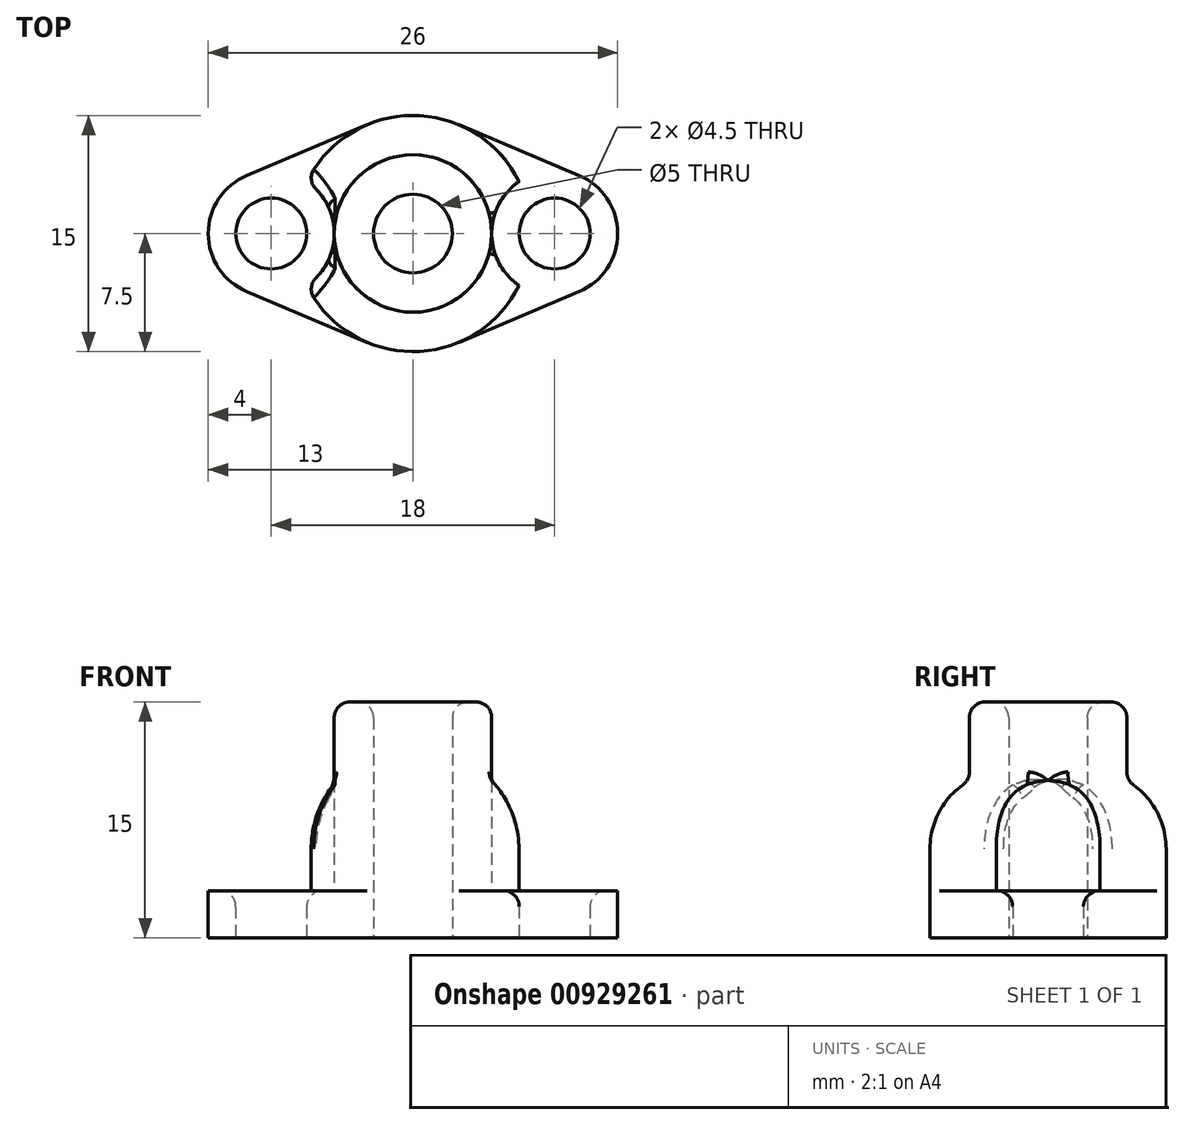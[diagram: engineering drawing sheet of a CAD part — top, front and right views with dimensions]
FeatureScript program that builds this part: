
annotation { "Feature Type Name" : "Feature", "Feature Type Description" : "" }
export const myFeature = defineFeature(function(context is Context, id is Id, definition is map)
    precondition{}
    {
        {
            var Q0;
            Q0=qCreatedBy(makeId("Top.planeOp"),FACE);
            var sketch = newSketch(context, id + "F0", { "sketchPlane" : qUnion([Q0])});
            skCircle(sketch, "E0", {"center": v(0, 0) * mm, "radius": 7.5 * mm});
            skCircle(sketch, "E1", {"center": v(0, 0) * mm, "radius": 5 * mm});
            skCircle(sketch, "E2", {"center": v(0, 0) * mm, "radius": 2.5 * mm});
            skCircle(sketch, "E3", {"center": v(-9, 0) * mm, "radius": 4 * mm});
            skLineSegment(sketch, "E4", {"start": v(-10.56, 3.69) * mm, "end": v(-2.92, 6.9) * mm});
            skLineSegment(sketch, "E5", {"start": v(-10.56, -3.69) * mm, "end": v(-2.92, -6.9) * mm});
            skLineSegment(sketch, "E6.MirrorCS", {"start": v(10.56, 3.69) * mm, "end": v(2.92, 6.9) * mm});
            skCircle(sketch, "E7.MirrorC", {"center": v(9, 0) * mm, "radius": 4 * mm});
            skLineSegment(sketch, "E8.MirrorCS", {"start": v(10.56, -3.69) * mm, "end": v(2.92, -6.9) * mm});
            skCircle(sketch, "E9", {"center": v(-9, 0) * mm, "radius": 2.25 * mm});
            skCircle(sketch, "E10.MirrorC", {"center": v(9, 0) * mm, "radius": 2.25 * mm});
            skSolve(sketch);
        }
        {
            var Q0;
            Q0=makeQuery(id+"F0.imprint","IMPRINT",FACE,{"disambiguationData":[TD([[makeQuery(id+"F0.imprint","IMPRINT",EDGE,{"derivedFrom":sQuery(id+"F0.wireOp",EDGE,"E1")}),1.0]])]});
            extrude(context, id + "F1", {"entities" : qUnion([Q0]), "depth" : 15 * mm, "offsetDistance" : 25 * mm});
        }
        {
            var Q0;
            Q0=makeQuery(id+"F0.imprint","IMPRINT",FACE,{"disambiguationData":[TD([[makeQuery(id+"F0.imprint","IMPRINT",EDGE,{"derivedFrom":sQuery(id+"F0.wireOp",EDGE,"E0")}),1.0]])]});
            extrude(context, id + "F2", {"entities" : qUnion([Q0]), "operationType" : NewBodyOperationType.ADD, "depth" : 10 * mm, "offsetDistance" : 25 * mm});
        }
        {
            var Q0;
            {var subQ0=sQuery(id+"F0.wireOp",EDGE,"E3");var subQ4=sQuery(id+"F0.wireOp",EDGE,"E0");var subQ7=makeQuery(id+"F0.imprint","INTERSECT",VERTEX,{"disambiguationData":[OD(0.0)],"derivedFrom":[subQ4,subQ0]});Q0=makeQuery(id+"F0.imprint","IMPRINT",FACE,{"disambiguationData":[TD([[makeQuery(id+"F0.imprint","IMPRINT",EDGE,{"disambiguationData":[TD([[subQ7,-1.0]])],"derivedFrom":subQ4}),-1.0]])]});}
            var Q1;
            {var subQ0=sQuery(id+"F0.wireOp",EDGE,"E3");var subQ1=sQuery(id+"F0.wireOp",EDGE,"E0");var subQ2=makeQuery(id+"F0.imprint","INTERSECT",VERTEX,{"disambiguationData":[OD(0.0)],"derivedFrom":[subQ1,subQ0]});Q1=makeQuery(id+"F0.imprint","IMPRINT",FACE,{"disambiguationData":[TD([[makeQuery(id+"F0.imprint","IMPRINT",EDGE,{"disambiguationData":[TD([[subQ2,-1.0]])],"derivedFrom":subQ1}),1.0]])]});}
            var Q2;
            {var subQ0=sQuery(id+"F0.wireOp",EDGE,"E5");Q2=makeQuery(id+"F0.imprint","IMPRINT",FACE,{"disambiguationData":[TD([[makeQuery(id+"F0.imprint","IMPRINT",EDGE,{"derivedFrom":subQ0}),1.0]])]});}
            var Q3;
            {var subQ0=sQuery(id+"F0.wireOp",EDGE,"E4");Q3=makeQuery(id+"F0.imprint","IMPRINT",FACE,{"disambiguationData":[TD([[makeQuery(id+"F0.imprint","IMPRINT",EDGE,{"derivedFrom":subQ0}),-1.0]])]});}
            var Q4;
            {var subQ0=sQuery(id+"F0.wireOp",EDGE,"E8.MirrorCS");Q4=makeQuery(id+"F0.imprint","IMPRINT",FACE,{"disambiguationData":[TD([[makeQuery(id+"F0.imprint","IMPRINT",EDGE,{"derivedFrom":subQ0}),-1.0]])]});}
            var Q5;
            {var subQ0=sQuery(id+"F0.wireOp",EDGE,"E7.MirrorC");var subQ2=sQuery(id+"F0.wireOp",EDGE,"E0");var subQ3=makeQuery(id+"F0.imprint","INTERSECT",VERTEX,{"disambiguationData":[OD(0.0)],"derivedFrom":[subQ2,subQ0]});Q5=makeQuery(id+"F0.imprint","IMPRINT",FACE,{"disambiguationData":[TD([[makeQuery(id+"F0.imprint","IMPRINT",EDGE,{"disambiguationData":[TD([[subQ3,1.0]])],"derivedFrom":subQ2}),-1.0]])]});}
            var Q6;
            {var subQ0=sQuery(id+"F0.wireOp",EDGE,"E7.MirrorC");var subQ1=sQuery(id+"F0.wireOp",EDGE,"E0");var subQ4=makeQuery(id+"F0.imprint","INTERSECT",VERTEX,{"disambiguationData":[OD(0.0)],"derivedFrom":[subQ1,subQ0]});Q6=makeQuery(id+"F0.imprint","IMPRINT",FACE,{"disambiguationData":[TD([[makeQuery(id+"F0.imprint","IMPRINT",EDGE,{"disambiguationData":[TD([[subQ4,1.0]])],"derivedFrom":subQ1}),1.0]])]});}
            var Q7;
            {var subQ0=sQuery(id+"F0.wireOp",EDGE,"E6.MirrorCS");Q7=makeQuery(id+"F0.imprint","IMPRINT",FACE,{"disambiguationData":[TD([[makeQuery(id+"F0.imprint","IMPRINT",EDGE,{"derivedFrom":subQ0}),1.0]])]});}
            extrude(context, id + "F3", {"entities" : qUnion([Q0, Q1, Q2, Q3, Q4, Q5, Q6, Q7]), "operationType" : NewBodyOperationType.ADD, "depth" : 3 * mm, "offsetDistance" : 25 * mm});
        }
        {
            var Q0;
            {var subQ0=sQuery(id+"F0.wireOp",EDGE,"E0");var subQ1=makeQuery(id+"F0.imprint","INTERSECT",VERTEX,{"derivedFrom":[subQ0,sQuery(id+"F0.wireOp",EDGE,"E8.MirrorCS")]});var subQ2=makeQuery(id+"F0.imprint","INTERSECT",VERTEX,{"derivedFrom":[subQ0,sQuery(id+"F0.wireOp",EDGE,"E5")]});Q0=makeQuery(id+"F2.opExtrude","CAP_EDGE",EDGE,{"disambiguationData":[OSD([subQ0]),TDD([makeQuery(id+"F0.imprint","IMPRINT",EDGE,{"disambiguationData":[TD([[subQ2,1.0]])],"derivedFrom":subQ0}),makeQuery(id+"F0.imprint","IMPRINT",EDGE,{"disambiguationData":[TD([[subQ2,-1.0]])],"derivedFrom":subQ0}),makeQuery(id+"F0.imprint","IMPRINT",EDGE,{"disambiguationData":[TD([[subQ1,-1.0]])],"derivedFrom":subQ0})])],"isStart":false});}
            var Q1;
            {var subQ0=sQuery(id+"F0.wireOp",EDGE,"E0");var subQ1=makeQuery(id+"F0.imprint","INTERSECT",VERTEX,{"derivedFrom":[subQ0,sQuery(id+"F0.wireOp",EDGE,"E4")]});var subQ2=makeQuery(id+"F0.imprint","INTERSECT",VERTEX,{"derivedFrom":[subQ0,sQuery(id+"F0.wireOp",EDGE,"E6.MirrorCS")]});Q1=makeQuery(id+"F2.opExtrude","CAP_EDGE",EDGE,{"disambiguationData":[OSD([subQ0]),TDD([makeQuery(id+"F0.imprint","IMPRINT",EDGE,{"disambiguationData":[TD([[subQ2,1.0]])],"derivedFrom":subQ0}),makeQuery(id+"F0.imprint","IMPRINT",EDGE,{"disambiguationData":[TD([[subQ1,1.0]])],"derivedFrom":subQ0}),makeQuery(id+"F0.imprint","IMPRINT",EDGE,{"disambiguationData":[TD([[subQ1,-1.0]])],"derivedFrom":subQ0})])],"isStart":false});}
            fillet(context, id + "F4", {"entities" : qUnion([Q0, Q1]), "radius" : 5 * mm, "tangentPropagation" : true, "allowEdgeOverflow" : false});
        }
        {
            var Q0;
            {var subQ0=sQuery(id+"F0.wireOp",EDGE,"E0");var subQ1=makeQuery(id+"F0.imprint","INTERSECT",VERTEX,{"derivedFrom":[subQ0,sQuery(id+"F0.wireOp",EDGE,"E4")]});var subQ2=makeQuery(id+"F0.imprint","INTERSECT",VERTEX,{"derivedFrom":[subQ0,sQuery(id+"F0.wireOp",EDGE,"E6.MirrorCS")]});Q0=makeQuery(id+"F4.opFillet","BLEND_EDGE",EDGE,{"blendedFrom":[makeQuery(id+"F2.opExtrude","CAP_EDGE",EDGE,{"disambiguationData":[OSD([subQ0]),TDD([makeQuery(id+"F0.imprint","IMPRINT",EDGE,{"disambiguationData":[TD([[subQ2,1.0]])],"derivedFrom":subQ0}),makeQuery(id+"F0.imprint","IMPRINT",EDGE,{"disambiguationData":[TD([[subQ1,1.0]])],"derivedFrom":subQ0}),makeQuery(id+"F0.imprint","IMPRINT",EDGE,{"disambiguationData":[TD([[subQ1,-1.0]])],"derivedFrom":subQ0})])],"isStart":false}),makeQuery(id+"F1.opExtrude","SWEPT_FACE",FACE,{"disambiguationData":[OSD([sQuery(id+"F0.wireOp",EDGE,"E1")])]})],"blendedInto":[makeQuery(id+"F1.opExtrude","SWEPT_FACE",FACE,{"disambiguationData":[OSD([sQuery(id+"F0.wireOp",EDGE,"E1")])]})]});}
            var Q1;
            {var subQ0=sQuery(id+"F0.wireOp",EDGE,"E0");Q1=makeQuery(id+"F3.opExtrude","CAP_EDGE",EDGE,{"disambiguationData":[OSD([subQ0]),TDD([makeQuery(id+"F0.imprint","IMPRINT",EDGE,{"disambiguationData":[TD([[makeQuery(id+"F0.imprint","INTERSECT",VERTEX,{"derivedFrom":[subQ0,sQuery(id+"F0.wireOp",EDGE,"E6.MirrorCS")]}),1.0]])],"derivedFrom":subQ0})])],"isStart":false});}
            var Q2;
            {var subQ0=sQuery(id+"F0.wireOp",EDGE,"E0");Q2=makeQuery(id+"F3.opExtrude","CAP_EDGE",EDGE,{"disambiguationData":[OSD([subQ0]),TDD([makeQuery(id+"F0.imprint","IMPRINT",EDGE,{"disambiguationData":[TD([[makeQuery(id+"F0.imprint","INTERSECT",VERTEX,{"derivedFrom":[subQ0,sQuery(id+"F0.wireOp",EDGE,"E4")]}),-1.0]])],"derivedFrom":subQ0})])],"isStart":false});}
            var Q3;
            {var subQ0=sQuery(id+"F0.wireOp",EDGE,"E0");Q3=makeQuery(id+"F3.opExtrude","CAP_EDGE",EDGE,{"disambiguationData":[OSD([subQ0]),TDD([makeQuery(id+"F0.imprint","IMPRINT",EDGE,{"disambiguationData":[TD([[makeQuery(id+"F0.imprint","INTERSECT",VERTEX,{"derivedFrom":[subQ0,sQuery(id+"F0.wireOp",EDGE,"E8.MirrorCS")]}),-1.0]])],"derivedFrom":subQ0})])],"isStart":false});}
            var Q4;
            {var subQ0=sQuery(id+"F0.wireOp",EDGE,"E0");Q4=makeQuery(id+"F3.opExtrude","CAP_EDGE",EDGE,{"disambiguationData":[OSD([subQ0]),TDD([makeQuery(id+"F0.imprint","IMPRINT",EDGE,{"disambiguationData":[TD([[makeQuery(id+"F0.imprint","INTERSECT",VERTEX,{"derivedFrom":[subQ0,sQuery(id+"F0.wireOp",EDGE,"E5")]}),1.0]])],"derivedFrom":subQ0})])],"isStart":false});}
            var Q5;
            Q5=makeQuery(id+"F1.opExtrude","CAP_EDGE",EDGE,{"disambiguationData":[OSD([sQuery(id+"F0.wireOp",EDGE,"E2")])],"isStart":false});
            var Q6;
            Q6=makeQuery(id+"F1.opExtrude","CAP_EDGE",EDGE,{"disambiguationData":[OSD([sQuery(id+"F0.wireOp",EDGE,"E1")])],"isStart":false});
            var Q7;
            Q7=makeQuery(id+"F3.opExtrude","CAP_EDGE",EDGE,{"disambiguationData":[OSD([sQuery(id+"F0.wireOp",EDGE,"E9")])],"isStart":false});
            var Q8;
            Q8=makeQuery(id+"F3.opExtrude","CAP_EDGE",EDGE,{"disambiguationData":[OSD([sQuery(id+"F0.wireOp",EDGE,"E10.MirrorC")])],"isStart":false});
            fillet(context, id + "F5", {"entities" : qUnion([Q0, Q1, Q2, Q3, Q4, Q5, Q6, Q7, Q8]), "radius" : 1 * mm, "tangentPropagation" : true, "allowEdgeOverflow" : false});
        }
        {
            var Q0;
            {var subQ0=sQuery(id+"F0.wireOp",EDGE,"E7.MirrorC");var subQ1=sQuery(id+"F0.wireOp",EDGE,"E0");var subQ3=makeQuery(id+"F0.imprint","INTERSECT",VERTEX,{"disambiguationData":[OD(0.0)],"derivedFrom":[subQ1,subQ0]});var subQ4=makeQuery(id+"F0.imprint","INTERSECT",VERTEX,{"derivedFrom":[subQ1,sQuery(id+"F0.wireOp",EDGE,"E4")]});var subQ5=makeQuery(id+"F0.imprint","INTERSECT",VERTEX,{"derivedFrom":[subQ1,sQuery(id+"F0.wireOp",EDGE,"E6.MirrorCS")]});Q0=makeQuery(id+"F4.opFillet","BLEND_EDGE",EDGE,{"blendedFrom":[makeQuery(id+"F2.opExtrude","CAP_EDGE",EDGE,{"disambiguationData":[OSD([subQ1]),TDD([makeQuery(id+"F0.imprint","IMPRINT",EDGE,{"disambiguationData":[TD([[subQ5,1.0]])],"derivedFrom":subQ1}),makeQuery(id+"F0.imprint","IMPRINT",EDGE,{"disambiguationData":[TD([[subQ4,1.0]])],"derivedFrom":subQ1}),makeQuery(id+"F0.imprint","IMPRINT",EDGE,{"disambiguationData":[TD([[subQ4,-1.0]])],"derivedFrom":subQ1})])],"isStart":false}),makeQuery(id+"F2.boolean.opBoolean","MERGE",FACE,{"derivedFrom":[makeQuery(id+"F2.opExtrude","SWEPT_FACE",FACE,{"disambiguationData":[OSD([subQ0]),TDD([makeQuery(id+"F0.imprint","IMPRINT",EDGE,{"disambiguationData":[TD([[subQ3,1.0]])],"derivedFrom":subQ0})])]}),makeQuery(id+"F2.opExtrude","SWEPT_FACE",FACE,{"disambiguationData":[OSD([subQ0]),TDD([makeQuery(id+"F0.imprint","IMPRINT",EDGE,{"disambiguationData":[TD([[makeQuery(id+"F0.imprint","INTERSECT",VERTEX,{"disambiguationData":[OD(1.0)],"derivedFrom":[subQ1,subQ0]}),-1.0]])],"derivedFrom":subQ0})])]})]})],"blendedInto":[makeQuery(id+"F2.boolean.opBoolean","MERGE",FACE,{"derivedFrom":[makeQuery(id+"F2.opExtrude","SWEPT_FACE",FACE,{"disambiguationData":[OSD([subQ0]),TDD([makeQuery(id+"F0.imprint","IMPRINT",EDGE,{"disambiguationData":[TD([[subQ3,1.0]])],"derivedFrom":subQ0})])]}),makeQuery(id+"F2.opExtrude","SWEPT_FACE",FACE,{"disambiguationData":[OSD([subQ0]),TDD([makeQuery(id+"F0.imprint","IMPRINT",EDGE,{"disambiguationData":[TD([[makeQuery(id+"F0.imprint","INTERSECT",VERTEX,{"disambiguationData":[OD(1.0)],"derivedFrom":[subQ1,subQ0]}),-1.0]])],"derivedFrom":subQ0})])]})]})]});}
            var Q1;
            {var subQ0=sQuery(id+"F0.wireOp",EDGE,"E7.MirrorC");var subQ1=sQuery(id+"F0.wireOp",EDGE,"E0");var subQ2=makeQuery(id+"F0.imprint","INTERSECT",VERTEX,{"disambiguationData":[OD(1.0)],"derivedFrom":[subQ1,subQ0]});var subQ4=makeQuery(id+"F0.imprint","INTERSECT",VERTEX,{"derivedFrom":[subQ1,sQuery(id+"F0.wireOp",EDGE,"E8.MirrorCS")]});var subQ5=makeQuery(id+"F0.imprint","INTERSECT",VERTEX,{"derivedFrom":[subQ1,sQuery(id+"F0.wireOp",EDGE,"E5")]});Q1=makeQuery(id+"F4.opFillet","BLEND_EDGE",EDGE,{"blendedFrom":[makeQuery(id+"F2.opExtrude","CAP_EDGE",EDGE,{"disambiguationData":[OSD([subQ1]),TDD([makeQuery(id+"F0.imprint","IMPRINT",EDGE,{"disambiguationData":[TD([[subQ5,1.0]])],"derivedFrom":subQ1}),makeQuery(id+"F0.imprint","IMPRINT",EDGE,{"disambiguationData":[TD([[subQ5,-1.0]])],"derivedFrom":subQ1}),makeQuery(id+"F0.imprint","IMPRINT",EDGE,{"disambiguationData":[TD([[subQ4,-1.0]])],"derivedFrom":subQ1})])],"isStart":false}),makeQuery(id+"F2.boolean.opBoolean","MERGE",FACE,{"derivedFrom":[makeQuery(id+"F2.opExtrude","SWEPT_FACE",FACE,{"disambiguationData":[OSD([subQ0]),TDD([makeQuery(id+"F0.imprint","IMPRINT",EDGE,{"disambiguationData":[TD([[makeQuery(id+"F0.imprint","INTERSECT",VERTEX,{"disambiguationData":[OD(0.0)],"derivedFrom":[subQ1,subQ0]}),1.0]])],"derivedFrom":subQ0})])]}),makeQuery(id+"F2.opExtrude","SWEPT_FACE",FACE,{"disambiguationData":[OSD([subQ0]),TDD([makeQuery(id+"F0.imprint","IMPRINT",EDGE,{"disambiguationData":[TD([[subQ2,-1.0]])],"derivedFrom":subQ0})])]})]})],"blendedInto":[makeQuery(id+"F2.boolean.opBoolean","MERGE",FACE,{"derivedFrom":[makeQuery(id+"F2.opExtrude","SWEPT_FACE",FACE,{"disambiguationData":[OSD([subQ0]),TDD([makeQuery(id+"F0.imprint","IMPRINT",EDGE,{"disambiguationData":[TD([[makeQuery(id+"F0.imprint","INTERSECT",VERTEX,{"disambiguationData":[OD(0.0)],"derivedFrom":[subQ1,subQ0]}),1.0]])],"derivedFrom":subQ0})])]}),makeQuery(id+"F2.opExtrude","SWEPT_FACE",FACE,{"disambiguationData":[OSD([subQ0]),TDD([makeQuery(id+"F0.imprint","IMPRINT",EDGE,{"disambiguationData":[TD([[subQ2,-1.0]])],"derivedFrom":subQ0})])]})]})]});}
            var Q2;
            {var subQ0=sQuery(id+"F0.wireOp",EDGE,"E3");var subQ1=sQuery(id+"F0.wireOp",EDGE,"E0");var subQ3=makeQuery(id+"F0.imprint","INTERSECT",VERTEX,{"disambiguationData":[OD(0.0)],"derivedFrom":[subQ1,subQ0]});var subQ4=makeQuery(id+"F0.imprint","INTERSECT",VERTEX,{"derivedFrom":[subQ1,sQuery(id+"F0.wireOp",EDGE,"E4")]});var subQ5=makeQuery(id+"F0.imprint","INTERSECT",VERTEX,{"derivedFrom":[subQ1,sQuery(id+"F0.wireOp",EDGE,"E6.MirrorCS")]});Q2=makeQuery(id+"F4.opFillet","BLEND_EDGE",EDGE,{"blendedFrom":[makeQuery(id+"F2.opExtrude","CAP_EDGE",EDGE,{"disambiguationData":[OSD([subQ1]),TDD([makeQuery(id+"F0.imprint","IMPRINT",EDGE,{"disambiguationData":[TD([[subQ5,1.0]])],"derivedFrom":subQ1}),makeQuery(id+"F0.imprint","IMPRINT",EDGE,{"disambiguationData":[TD([[subQ4,1.0]])],"derivedFrom":subQ1}),makeQuery(id+"F0.imprint","IMPRINT",EDGE,{"disambiguationData":[TD([[subQ4,-1.0]])],"derivedFrom":subQ1})])],"isStart":false}),makeQuery(id+"F2.boolean.opBoolean","MERGE",FACE,{"derivedFrom":[makeQuery(id+"F2.opExtrude","SWEPT_FACE",FACE,{"disambiguationData":[OSD([subQ0]),TDD([makeQuery(id+"F0.imprint","IMPRINT",EDGE,{"disambiguationData":[TD([[subQ3,1.0]])],"derivedFrom":subQ0})])]}),makeQuery(id+"F2.opExtrude","SWEPT_FACE",FACE,{"disambiguationData":[OSD([subQ0]),TDD([makeQuery(id+"F0.imprint","IMPRINT",EDGE,{"disambiguationData":[TD([[makeQuery(id+"F0.imprint","INTERSECT",VERTEX,{"disambiguationData":[OD(1.0)],"derivedFrom":[subQ1,subQ0]}),-1.0]])],"derivedFrom":subQ0})])]})]})],"blendedInto":[makeQuery(id+"F2.boolean.opBoolean","MERGE",FACE,{"derivedFrom":[makeQuery(id+"F2.opExtrude","SWEPT_FACE",FACE,{"disambiguationData":[OSD([subQ0]),TDD([makeQuery(id+"F0.imprint","IMPRINT",EDGE,{"disambiguationData":[TD([[subQ3,1.0]])],"derivedFrom":subQ0})])]}),makeQuery(id+"F2.opExtrude","SWEPT_FACE",FACE,{"disambiguationData":[OSD([subQ0]),TDD([makeQuery(id+"F0.imprint","IMPRINT",EDGE,{"disambiguationData":[TD([[makeQuery(id+"F0.imprint","INTERSECT",VERTEX,{"disambiguationData":[OD(1.0)],"derivedFrom":[subQ1,subQ0]}),-1.0]])],"derivedFrom":subQ0})])]})]})]});}
            var Q3;
            {var subQ0=sQuery(id+"F0.wireOp",EDGE,"E3");var subQ1=sQuery(id+"F0.wireOp",EDGE,"E0");var subQ2=makeQuery(id+"F0.imprint","INTERSECT",VERTEX,{"disambiguationData":[OD(1.0)],"derivedFrom":[subQ1,subQ0]});var subQ4=makeQuery(id+"F0.imprint","INTERSECT",VERTEX,{"derivedFrom":[subQ1,sQuery(id+"F0.wireOp",EDGE,"E8.MirrorCS")]});var subQ5=makeQuery(id+"F0.imprint","INTERSECT",VERTEX,{"derivedFrom":[subQ1,sQuery(id+"F0.wireOp",EDGE,"E5")]});Q3=makeQuery(id+"F4.opFillet","BLEND_EDGE",EDGE,{"blendedFrom":[makeQuery(id+"F2.opExtrude","CAP_EDGE",EDGE,{"disambiguationData":[OSD([subQ1]),TDD([makeQuery(id+"F0.imprint","IMPRINT",EDGE,{"disambiguationData":[TD([[subQ5,1.0]])],"derivedFrom":subQ1}),makeQuery(id+"F0.imprint","IMPRINT",EDGE,{"disambiguationData":[TD([[subQ5,-1.0]])],"derivedFrom":subQ1}),makeQuery(id+"F0.imprint","IMPRINT",EDGE,{"disambiguationData":[TD([[subQ4,-1.0]])],"derivedFrom":subQ1})])],"isStart":false}),makeQuery(id+"F2.boolean.opBoolean","MERGE",FACE,{"derivedFrom":[makeQuery(id+"F2.opExtrude","SWEPT_FACE",FACE,{"disambiguationData":[OSD([subQ0]),TDD([makeQuery(id+"F0.imprint","IMPRINT",EDGE,{"disambiguationData":[TD([[makeQuery(id+"F0.imprint","INTERSECT",VERTEX,{"disambiguationData":[OD(0.0)],"derivedFrom":[subQ1,subQ0]}),1.0]])],"derivedFrom":subQ0})])]}),makeQuery(id+"F2.opExtrude","SWEPT_FACE",FACE,{"disambiguationData":[OSD([subQ0]),TDD([makeQuery(id+"F0.imprint","IMPRINT",EDGE,{"disambiguationData":[TD([[subQ2,-1.0]])],"derivedFrom":subQ0})])]})]})],"blendedInto":[makeQuery(id+"F2.boolean.opBoolean","MERGE",FACE,{"derivedFrom":[makeQuery(id+"F2.opExtrude","SWEPT_FACE",FACE,{"disambiguationData":[OSD([subQ0]),TDD([makeQuery(id+"F0.imprint","IMPRINT",EDGE,{"disambiguationData":[TD([[makeQuery(id+"F0.imprint","INTERSECT",VERTEX,{"disambiguationData":[OD(0.0)],"derivedFrom":[subQ1,subQ0]}),1.0]])],"derivedFrom":subQ0})])]}),makeQuery(id+"F2.opExtrude","SWEPT_FACE",FACE,{"disambiguationData":[OSD([subQ0]),TDD([makeQuery(id+"F0.imprint","IMPRINT",EDGE,{"disambiguationData":[TD([[subQ2,-1.0]])],"derivedFrom":subQ0})])]})]})]});}
            fillet(context, id + "F6", {"entities" : qUnion([Q0, Q1, Q2, Q3]), "radius" : 1 * mm, "tangentPropagation" : true, "allowEdgeOverflow" : false});
        }
    });
